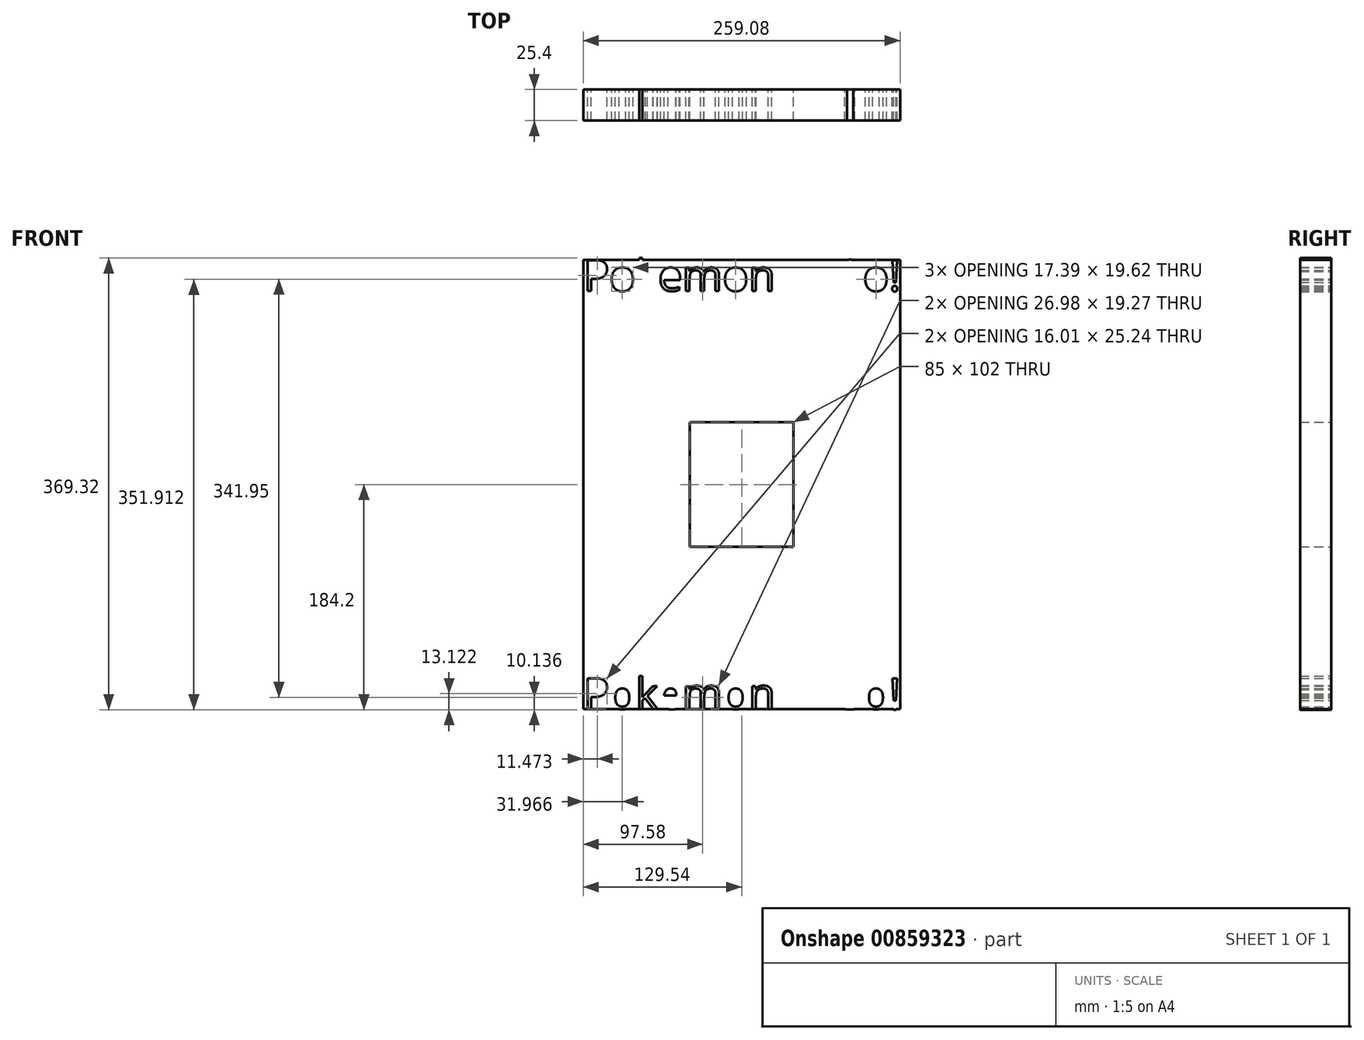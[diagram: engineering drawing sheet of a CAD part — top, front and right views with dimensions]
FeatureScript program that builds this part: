
annotation { "Feature Type Name" : "Feature", "Feature Type Description" : "" }
export const myFeature = defineFeature(function(context is Context, id is Id, definition is map)
    precondition{}
    {
        {
            var Q0;
            Q0=qCreatedBy(makeId("Front.planeOp"),FACE);
            var sketch = newSketch(context, id + "F0", { "sketchPlane" : qUnion([Q0])});
            skLineSegment(sketch, "E0.bottom", {"start": v(-129.54, 183.7) * mm, "end": v(129.54, 183.7) * mm});
            skLineSegment(sketch, "E0.top", {"start": v(-129.54, -183.7) * mm, "end": v(129.54, -183.7) * mm});
            skLineSegment(sketch, "E0.left", {"start": v(-129.54, 183.7) * mm, "end": v(-129.54, -183.7) * mm});
            skLineSegment(sketch, "E0.right", {"start": v(129.54, 183.7) * mm, "end": v(129.54, -183.7) * mm});
            skPoint(sketch, "E0.middle", {"position": v(0, 0) * mm});
            skLineSegment(sketch, "E1.bottom", {"start": v(-42.5, 51) * mm, "end": v(42.5, 51) * mm});
            skLineSegment(sketch, "E1.top", {"start": v(-42.5, -51) * mm, "end": v(42.5, -51) * mm});
            skLineSegment(sketch, "E1.left", {"start": v(-42.5, 51) * mm, "end": v(-42.5, -51) * mm});
            skLineSegment(sketch, "E1.right", {"start": v(42.5, 51) * mm, "end": v(42.5, -51) * mm});
            skText(sketch, "E2", { "text": "Pokemon     Go!", "fontName": "OpenSans-Regular.ttf"});
            skText(sketch, "E3", { "text": "Pokemon     Go!", "fontName": "OpenSans-Regular.ttf"});
            const initialGuessF0  = {"E2": [-0.12954, 0.15825, 1, 0, 0.02546], "E3": [-0.12954, -0.1837, 1, 0, 0.02546]};
            skSetInitialGuess(sketch, initialGuessF0);
            skSolve(sketch);
        }
        {
            var Q0;
            Q0 = qSketchRegion(id + "F0", true);
            extrude(context, id + "F1", {"entities" : qUnion([Q0]), "depth" : 25.4 * mm, "offsetDistance" : 25.4 * mm});
        }
    });
